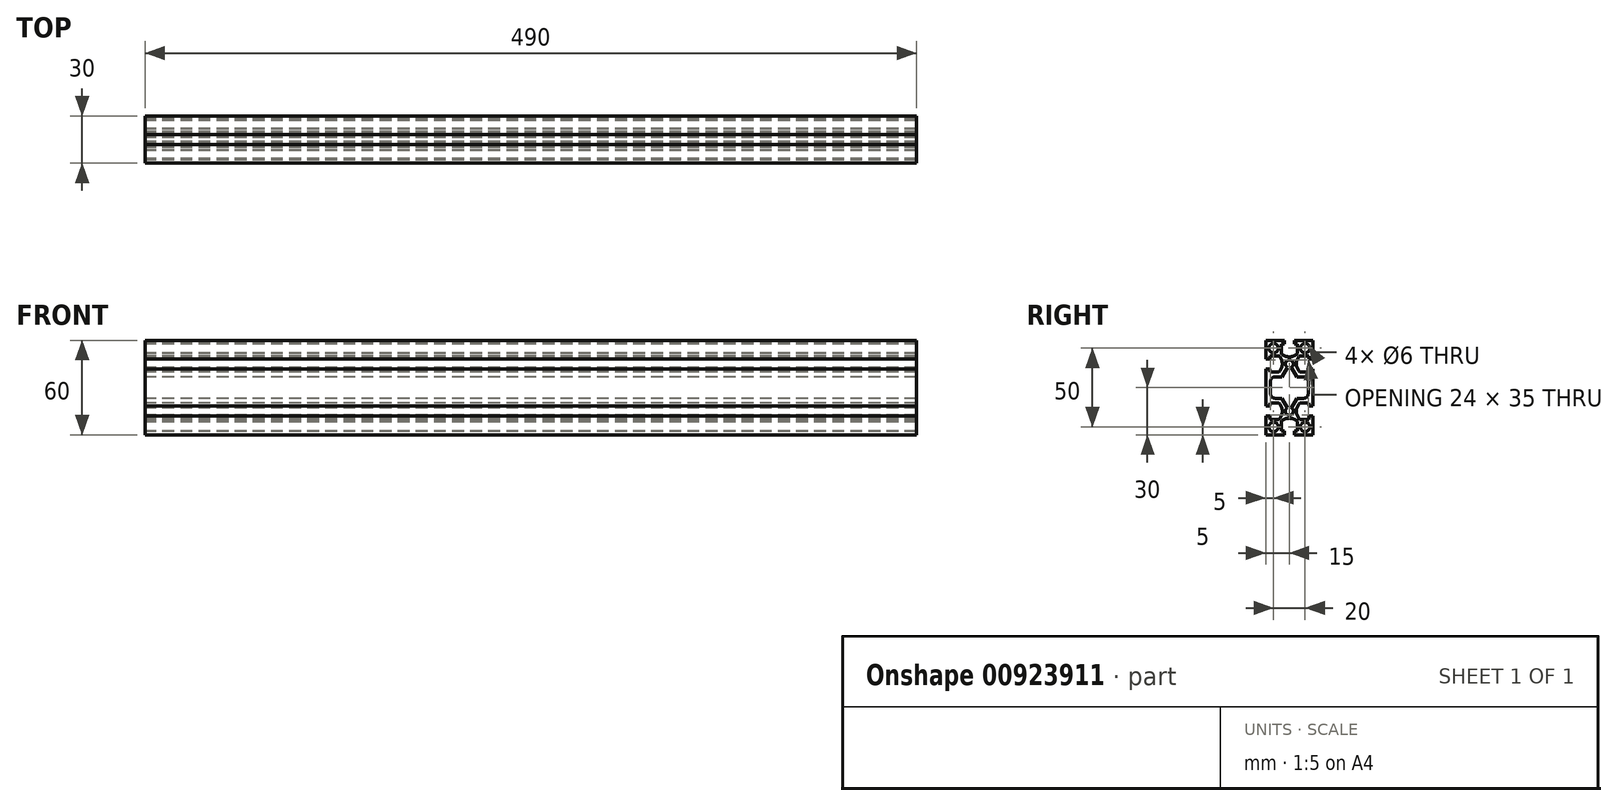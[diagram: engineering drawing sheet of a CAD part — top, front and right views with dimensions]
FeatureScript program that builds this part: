
annotation { "Feature Type Name" : "Feature", "Feature Type Description" : "" }
export const myFeature = defineFeature(function(context is Context, id is Id, definition is map)
    precondition{}
    {
        {
            var Q0;
            Q0=qCreatedBy(makeId("Right.planeOp"),FACE);
            var sketch = newSketch(context, id + "F0", { "sketchPlane" : qUnion([Q0])});
            skArc(sketch, "E0", {"start": v(-9, 6.85) * mm, "mid": v(-11.12, 5.97) * mm, "end": v(-12, 3.85) * mm});
            skLineSegment(sketch, "E1", {"start": v(-9, 6.85) * mm, "end": v(-4.7, 6.85) * mm});
            skLineSegment(sketch, "E2", {"start": v(-4.7, 6.85) * mm, "end": v(-1.25, 12.83) * mm});
            skArc(sketch, "E3", {"start": v(1.25, 12.83) * mm, "mid": v(0, 17.5) * mm, "end": v(-1.25, 12.83) * mm});
            skLineSegment(sketch, "E4", {"start": v(1.25, 12.83) * mm, "end": v(4.7, 6.85) * mm});
            skLineSegment(sketch, "E5", {"start": v(4.7, 6.85) * mm, "end": v(9, 6.85) * mm});
            skArc(sketch, "E6", {"start": v(12, 3.85) * mm, "mid": v(11.12, 5.97) * mm, "end": v(9, 6.85) * mm});
            skLineSegment(sketch, "E7", {"start": v(12, 3.85) * mm, "end": v(12, -3.85) * mm});
            skArc(sketch, "E8", {"start": v(9, -6.85) * mm, "mid": v(11.12, -5.97) * mm, "end": v(12, -3.85) * mm});
            skLineSegment(sketch, "E9", {"start": v(9, -6.85) * mm, "end": v(4.7, -6.85) * mm});
            skLineSegment(sketch, "E10", {"start": v(4.7, -6.85) * mm, "end": v(1.25, -12.83) * mm});
            skArc(sketch, "E11", {"start": v(-1.25, -12.83) * mm, "mid": v(0, -17.5) * mm, "end": v(1.25, -12.83) * mm});
            skLineSegment(sketch, "E12", {"start": v(-1.25, -12.83) * mm, "end": v(-4.7, -6.85) * mm});
            skLineSegment(sketch, "E13", {"start": v(-4.7, -6.85) * mm, "end": v(-9, -6.85) * mm});
            skArc(sketch, "E14", {"start": v(-12, -3.85) * mm, "mid": v(-11.12, -5.97) * mm, "end": v(-9, -6.85) * mm});
            skLineSegment(sketch, "E15", {"start": v(-12, -3.85) * mm, "end": v(-12, 3.85) * mm});
            skCircle(sketch, "E16", {"center": v(-10, 25) * mm, "radius": 3 * mm});
            skCircle(sketch, "E17", {"center": v(10, 25) * mm, "radius": 3 * mm});
            skCircle(sketch, "E18", {"center": v(-10, -25) * mm, "radius": 3 * mm});
            skCircle(sketch, "E19", {"center": v(10, -25) * mm, "radius": 3 * mm});
            skLineSegment(sketch, "E20", {"start": v(15, -11.85) * mm, "end": v(12.5, -11.85) * mm});
            skLineSegment(sketch, "E21", {"start": v(12.5, -11.85) * mm, "end": v(12.5, -9.85) * mm});
            skLineSegment(sketch, "E22", {"start": v(12.5, -9.85) * mm, "end": v(6.55, -9.85) * mm});
            skArc(sketch, "E23", {"start": v(6.55, -9.85) * mm, "mid": v(4.5, -15) * mm, "end": v(6.55, -20.15) * mm});
            skLineSegment(sketch, "E24", {"start": v(6.55, -20.15) * mm, "end": v(12.5, -20.15) * mm});
            skLineSegment(sketch, "E25", {"start": v(12.5, -20.15) * mm, "end": v(12.5, -18.15) * mm});
            skLineSegment(sketch, "E26", {"start": v(12.5, -18.15) * mm, "end": v(15, -18.15) * mm});
            skLineSegment(sketch, "E27", {"start": v(15, -18.15) * mm, "end": v(15, -30) * mm});
            skLineSegment(sketch, "E28", {"start": v(15, -30) * mm, "end": v(3.15, -30) * mm});
            skLineSegment(sketch, "E29", {"start": v(3.15, -30) * mm, "end": v(3.15, -27.5) * mm});
            skLineSegment(sketch, "E30", {"start": v(3.15, -27.5) * mm, "end": v(5.15, -27.5) * mm});
            skLineSegment(sketch, "E31", {"start": v(5.15, -27.5) * mm, "end": v(5.15, -21.55) * mm});
            skArc(sketch, "E32", {"start": v(5.15, -21.55) * mm, "mid": v(0, -19.5) * mm, "end": v(-5.15, -21.55) * mm});
            skLineSegment(sketch, "E33", {"start": v(-5.15, -21.55) * mm, "end": v(-5.15, -27.5) * mm});
            skLineSegment(sketch, "E34", {"start": v(-5.15, -27.5) * mm, "end": v(-3.15, -27.5) * mm});
            skLineSegment(sketch, "E35", {"start": v(-3.15, -27.5) * mm, "end": v(-3.15, -30) * mm});
            skLineSegment(sketch, "E36", {"start": v(-3.15, -30) * mm, "end": v(-15, -30) * mm});
            skLineSegment(sketch, "E37", {"start": v(-15, -30) * mm, "end": v(-15, -18.15) * mm});
            skLineSegment(sketch, "E38", {"start": v(-15, -18.15) * mm, "end": v(-12.5, -18.15) * mm});
            skLineSegment(sketch, "E39", {"start": v(-12.5, -18.15) * mm, "end": v(-12.5, -20.15) * mm});
            skLineSegment(sketch, "E40", {"start": v(-12.5, -20.15) * mm, "end": v(-6.55, -20.15) * mm});
            skArc(sketch, "E41", {"start": v(-6.55, -20.15) * mm, "mid": v(-4.5, -15) * mm, "end": v(-6.55, -9.85) * mm});
            skLineSegment(sketch, "E42", {"start": v(-6.55, -9.85) * mm, "end": v(-12.5, -9.85) * mm});
            skLineSegment(sketch, "E43", {"start": v(-12.5, -9.85) * mm, "end": v(-12.5, -11.85) * mm});
            skLineSegment(sketch, "E44", {"start": v(-12.5, -11.85) * mm, "end": v(-15, -11.85) * mm});
            skLineSegment(sketch, "E45", {"start": v(-15, -11.85) * mm, "end": v(-15, 11.85) * mm});
            skLineSegment(sketch, "E46", {"start": v(-15, 11.85) * mm, "end": v(-12.5, 11.85) * mm});
            skLineSegment(sketch, "E47", {"start": v(-12.5, 11.85) * mm, "end": v(-12.5, 9.85) * mm});
            skLineSegment(sketch, "E48", {"start": v(-12.5, 9.85) * mm, "end": v(-6.55, 9.85) * mm});
            skArc(sketch, "E49", {"start": v(-6.55, 9.85) * mm, "mid": v(-4.5, 15) * mm, "end": v(-6.55, 20.15) * mm});
            skLineSegment(sketch, "E50", {"start": v(-6.55, 20.15) * mm, "end": v(-12.5, 20.15) * mm});
            skLineSegment(sketch, "E51", {"start": v(-12.5, 20.15) * mm, "end": v(-12.5, 18.15) * mm});
            skLineSegment(sketch, "E52", {"start": v(-12.5, 18.15) * mm, "end": v(-15, 18.15) * mm});
            skLineSegment(sketch, "E53", {"start": v(-15, 18.15) * mm, "end": v(-15, 30) * mm});
            skLineSegment(sketch, "E54", {"start": v(-15, 30) * mm, "end": v(-3.15, 30) * mm});
            skLineSegment(sketch, "E55", {"start": v(-3.15, 30) * mm, "end": v(-3.15, 27.5) * mm});
            skLineSegment(sketch, "E56", {"start": v(-3.15, 27.5) * mm, "end": v(-5.15, 27.5) * mm});
            skLineSegment(sketch, "E57", {"start": v(-5.15, 27.5) * mm, "end": v(-5.15, 21.55) * mm});
            skArc(sketch, "E58", {"start": v(-5.15, 21.55) * mm, "mid": v(0, 19.5) * mm, "end": v(5.15, 21.55) * mm});
            skLineSegment(sketch, "E59", {"start": v(5.15, 21.55) * mm, "end": v(5.15, 27.5) * mm});
            skLineSegment(sketch, "E60", {"start": v(5.15, 27.5) * mm, "end": v(3.15, 27.5) * mm});
            skLineSegment(sketch, "E61", {"start": v(3.15, 27.5) * mm, "end": v(3.15, 30) * mm});
            skLineSegment(sketch, "E62", {"start": v(3.15, 30) * mm, "end": v(15, 30) * mm});
            skLineSegment(sketch, "E63", {"start": v(15, 30) * mm, "end": v(15, 18.15) * mm});
            skLineSegment(sketch, "E64", {"start": v(15, 18.15) * mm, "end": v(12.5, 18.15) * mm});
            skLineSegment(sketch, "E65", {"start": v(12.5, 18.15) * mm, "end": v(12.5, 20.15) * mm});
            skLineSegment(sketch, "E66", {"start": v(12.5, 20.15) * mm, "end": v(6.55, 20.15) * mm});
            skArc(sketch, "E67", {"start": v(6.55, 20.15) * mm, "mid": v(4.5, 15) * mm, "end": v(6.55, 9.85) * mm});
            skLineSegment(sketch, "E68", {"start": v(6.55, 9.85) * mm, "end": v(12.5, 9.85) * mm});
            skLineSegment(sketch, "E69", {"start": v(12.5, 9.85) * mm, "end": v(12.5, 11.85) * mm});
            skLineSegment(sketch, "E70", {"start": v(12.5, 11.85) * mm, "end": v(15, 11.85) * mm});
            skLineSegment(sketch, "E71", {"start": v(15, 11.85) * mm, "end": v(15, -11.85) * mm});
            skSolve(sketch);
        }
        {
            var Q0;
            Q0=qSketchRegion(id+"F0",true);
            extrude(context, id + "F1", {"entities" : qUnion([Q0]), "depth" : 490 * mm, "offsetDistance" : 25 * mm});
        }
    });
